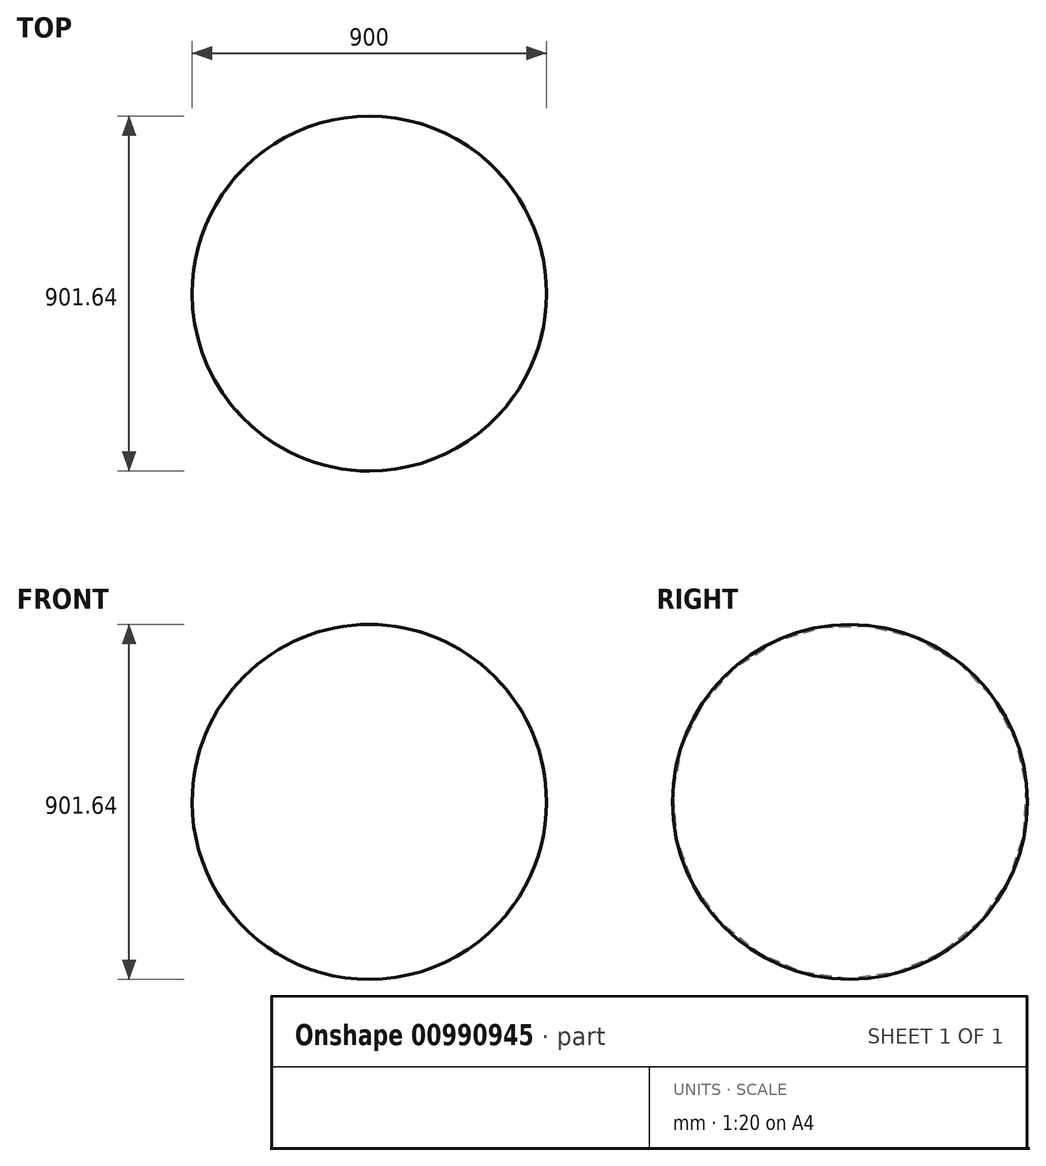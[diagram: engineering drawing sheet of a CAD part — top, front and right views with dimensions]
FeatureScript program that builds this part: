
annotation { "Feature Type Name" : "Feature", "Feature Type Description" : "" }
export const myFeature = defineFeature(function(context is Context, id is Id, definition is map)
    precondition{}
    {
        {
            var Q0;
            Q0=qCreatedBy(makeId("Top.planeOp"),FACE);
            var sketch = newSketch(context, id + "F0", { "sketchPlane" : qUnion([Q0])});
            skLineSegment(sketch, "E0", {"start": v(0, 0) * mm, "end": v(900, 0) * mm});
            skArc(sketch, "E1", {"start": v(900, 0) * mm, "mid": v(450, 450.82) * mm, "end": v(0, 0) * mm});
            skLineSegment(sketch, "E2", {"start": v(126.18, 313.3) * mm, "end": v(126.18, 0) * mm});
            skSolve(sketch);
        }
        {
            var Q0;
            Q0=makeQuery(id+"F0.imprint","IMPRINT",FACE,{"disambiguationData":[TD([[makeQuery(id+"F0.imprint","IMPRINT",EDGE,{"derivedFrom":sQuery(id+"F0.wireOp",EDGE,"E0")}),1.0]])]});
            var Q1;
            Q1=sQuery(id+"F0.wireOp",EDGE,"E0");
            revolve(context, id + "F1", {"surfaceOperationType" : NewSurfaceOperationType.NEW, "entities" : qUnion([Q0]), "axis" : qUnion([Q1]), "revolveType" : RevolveType.FULL});
        }
    });
